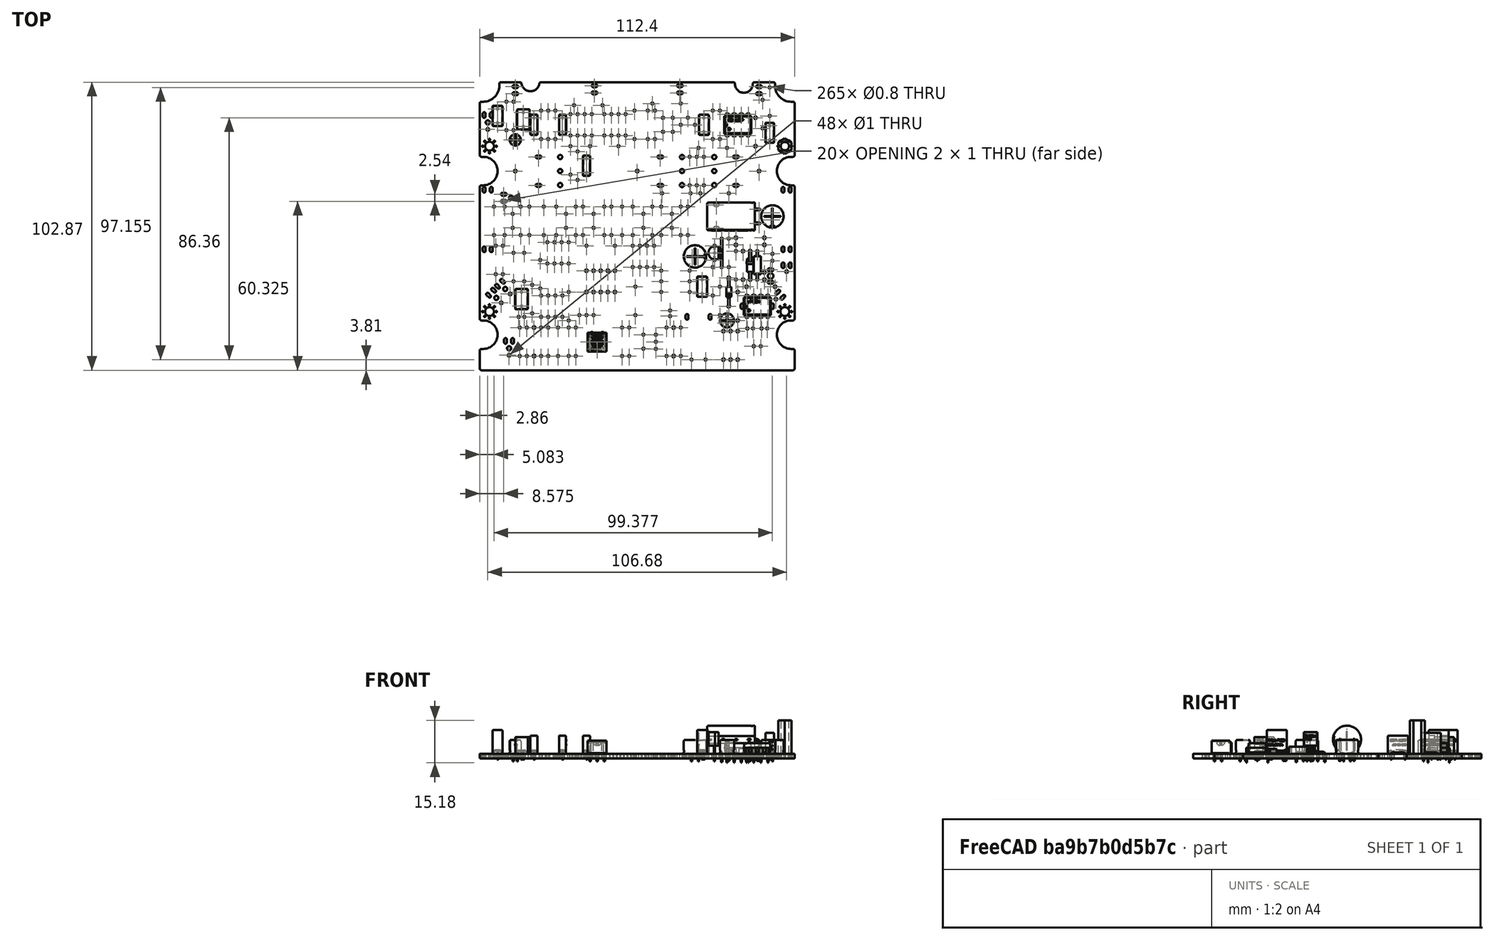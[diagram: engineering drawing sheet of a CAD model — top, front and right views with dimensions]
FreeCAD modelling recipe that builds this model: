
FCSTD DOCUMENT  (FreeCAD 0.19R17089 +1543 (Git))
Label: #100-000 - Phasor PCB Assembly
License: All rights reserved
LicenseURL: http://en.wikipedia.org/wiki/All_rights_reserved
objects: App::Link×103, Part::Feature×25, App::Part×7, PartDesign::CoordinateSystem×1, Sketcher::SketchObject×1
note: 27 computed .brp shape members not serialized (recipe doc carries the construction recipe); baked Part::Feature solids carry a one-line shape summary decoded from their .brp

FEATURE [PartDesign::CoordinateSystem] Local_CS_3323
  AttacherType = Attacher::AttachEngine3D
FEATURE [Part::Feature] Pcb_3323
  Placement = pos=(-147.637,134.62,0) rot=(0,0,1;0rad)
  shape: bbox 112.4 x 102.9 x 1.6 mm, 679 faces (baked)
FEATURE [Sketcher::SketchObject] PCB_Sketch_3323
  sketch-geometry (49):
    g0: LineSegment StartX=48.5775 StartY=90.17 StartZ=0 EndX=41.91 EndY=90.17 EndZ=0
    g1: LineSegment StartX=-41.91 StartY=90.17 StartZ=0 EndX=-48.5775 EndY=90.17 EndZ=0
    g2: LineSegment StartX=-56.1975 StartY=64.135 StartZ=0 EndX=-56.1975 EndY=82.55 EndZ=0
    g3: LineSegment StartX=56.1975 StartY=5.715 StartZ=0 EndX=56.1975 EndY=52.705 EndZ=0
    g4: LineSegment StartX=54.9275 StartY=53.34 StartZ=0 EndX=55.5625 EndY=53.34 EndZ=0
    g5: LineSegment StartX=54.9275 StartY=63.5 StartZ=0 EndX=55.5625 EndY=63.5 EndZ=0
    g6: LineSegment StartX=-54.9275 StartY=63.5 StartZ=0 EndX=-55.5625 EndY=63.5 EndZ=0
    g7: LineSegment StartX=-54.9275 StartY=53.34 StartZ=0 EndX=-55.5625 EndY=53.34 EndZ=0
    g8: LineSegment StartX=-54.9275 StartY=5.08 StartZ=0 EndX=-55.5625 EndY=5.08 EndZ=0
    g9: LineSegment StartX=49.2125 StartY=89.535 StartZ=0 EndX=49.2125 EndY=88.9 EndZ=0
    g10: LineSegment StartX=55.5625 StartY=83.185 StartZ=0 EndX=54.9275 EndY=83.185 EndZ=0
    g11: LineSegment StartX=55.5625 StartY=5.08 StartZ=0 EndX=54.9275 EndY=5.08 EndZ=0
    g12: LineSegment StartX=55.5625 StartY=-5.08 StartZ=0 EndX=54.9275 EndY=-5.08 EndZ=0
    g13: LineSegment StartX=-54.9275 StartY=-12.7 StartZ=0 EndX=-55.5625 EndY=-12.7 EndZ=0
    g14: LineSegment StartX=-54.9275 StartY=-5.08 StartZ=0 EndX=-55.5625 EndY=-5.08 EndZ=0
    g15: LineSegment StartX=-54.9275 StartY=83.185 StartZ=0 EndX=-55.5625 EndY=83.185 EndZ=0
    g16: LineSegment StartX=-49.2125 StartY=88.9 StartZ=0 EndX=-49.2125 EndY=89.535 EndZ=0
    g17: LineSegment StartX=-56.1975 StartY=-5.715 StartZ=0 EndX=-56.1975 EndY=-12.065 EndZ=0
    g18: LineSegment StartX=56.1975 StartY=-5.715 StartZ=0 EndX=56.1975 EndY=-12.065 EndZ=0
    g19: LineSegment StartX=34.29 StartY=90.17 StartZ=0 EndX=-34.29 EndY=90.17 EndZ=0
    g20: LineSegment StartX=56.1975 StartY=64.135 StartZ=0 EndX=56.1975 EndY=82.55 EndZ=0
    g21: LineSegment StartX=-54.9275 StartY=-12.7 StartZ=0 EndX=55.5625 EndY=-12.7 EndZ=0
    g22: LineSegment StartX=-56.1975 StartY=5.715 StartZ=0 EndX=-56.1975 EndY=52.705 EndZ=0
    g23: ArcOfCircle CenterX=-55.5625 CenterY=82.55 CenterZ=0 NormalX=0 NormalY=0 NormalZ=1 AngleXU=0 Radius=0.635 StartAngle=1.5708 EndAngle=3.14159
    g24: ArcOfCircle CenterX=-55.5625 CenterY=64.135 CenterZ=0 NormalX=0 NormalY=0 NormalZ=1 AngleXU=0 Radius=0.635 StartAngle=3.14159 EndAngle=4.71239
    g25: ArcOfCircle CenterX=-55.5625 CenterY=52.705 CenterZ=0 NormalX=0 NormalY=0 NormalZ=1 AngleXU=0 Radius=0.635 StartAngle=1.5708 EndAngle=3.14159
    g26: ArcOfCircle CenterX=-55.5625 CenterY=5.715 CenterZ=0 NormalX=0 NormalY=0 NormalZ=1 AngleXU=0 Radius=0.635 StartAngle=3.14159 EndAngle=4.71239
    g27: ArcOfCircle CenterX=-55.5625 CenterY=-5.715 CenterZ=0 NormalX=0 NormalY=0 NormalZ=1 AngleXU=0 Radius=0.635 StartAngle=1.5708 EndAngle=3.14159
    g28: ArcOfCircle CenterX=-55.5625 CenterY=-12.065 CenterZ=0 NormalX=0 NormalY=0 NormalZ=1 AngleXU=0 Radius=0.635 StartAngle=3.14159 EndAngle=4.71239
    g29: ArcOfCircle CenterX=55.5625 CenterY=-12.065 CenterZ=0 NormalX=0 NormalY=0 NormalZ=1 AngleXU=0 Radius=0.635 StartAngle=4.71239 EndAngle=6.28319
    g30: ArcOfCircle CenterX=55.5625 CenterY=-5.715 CenterZ=0 NormalX=0 NormalY=0 NormalZ=1 AngleXU=0 Radius=0.635 StartAngle=0 EndAngle=1.5708
    g31: ArcOfCircle CenterX=55.5625 CenterY=5.715 CenterZ=0 NormalX=0 NormalY=0 NormalZ=1 AngleXU=0 Radius=0.635 StartAngle=4.71239 EndAngle=6.28319
    g32: ArcOfCircle CenterX=55.5625 CenterY=52.705 CenterZ=0 NormalX=0 NormalY=0 NormalZ=1 AngleXU=0 Radius=0.635 StartAngle=0 EndAngle=1.5708
    g33: ArcOfCircle CenterX=55.5625 CenterY=64.135 CenterZ=0 NormalX=0 NormalY=0 NormalZ=1 AngleXU=0 Radius=0.635 StartAngle=4.71239 EndAngle=6.28319
    g34: ArcOfCircle CenterX=55.5625 CenterY=82.55 CenterZ=0 NormalX=0 NormalY=0 NormalZ=1 AngleXU=0 Radius=0.635 StartAngle=0 EndAngle=1.5708
    g35: ArcOfCircle CenterX=48.5775 CenterY=89.535 CenterZ=0 NormalX=0 NormalY=0 NormalZ=1 AngleXU=0 Radius=0.635 StartAngle=0 EndAngle=1.5708
    g36: ArcOfCircle CenterX=41.91 CenterY=89.535 CenterZ=0 NormalX=0 NormalY=0 NormalZ=1 AngleXU=0 Radius=0.635 StartAngle=1.5708 EndAngle=3.14159
    g37: ArcOfCircle CenterX=34.29 CenterY=89.535 CenterZ=0 NormalX=0 NormalY=0 NormalZ=1 AngleXU=0 Radius=0.635 StartAngle=0 EndAngle=1.5708
    g38: ArcOfCircle CenterX=-34.29 CenterY=89.535 CenterZ=0 NormalX=0 NormalY=0 NormalZ=1 AngleXU=0 Radius=0.635 StartAngle=1.5708 EndAngle=3.14159
    g39: ArcOfCircle CenterX=-41.91 CenterY=89.535 CenterZ=0 NormalX=0 NormalY=0 NormalZ=1 AngleXU=0 Radius=0.635 StartAngle=0 EndAngle=1.5708
    g40: ArcOfCircle CenterX=-48.5775 CenterY=89.535 CenterZ=0 NormalX=0 NormalY=0 NormalZ=1 AngleXU=0 Radius=0.635 StartAngle=1.5708 EndAngle=3.14159
    g41: ArcOfCircle CenterX=38.1 CenterY=89.535 CenterZ=0 NormalX=0 NormalY=0 NormalZ=1 AngleXU=0 Radius=3.175 StartAngle=3.14159 EndAngle=6.28319
    g42: ArcOfCircle CenterX=-38.1 CenterY=90.17 CenterZ=0 NormalX=0 NormalY=0 NormalZ=1 AngleXU=0 Radius=3.23788 StartAngle=3.33899 EndAngle=6.08579
    g43: ArcOfCircle CenterX=54.9275 CenterY=58.42 CenterZ=0 NormalX=0 NormalY=0 NormalZ=1 AngleXU=0 Radius=5.08 StartAngle=1.5708 EndAngle=4.71239
    g44: ArcOfCircle CenterX=-54.9275 CenterY=58.42 CenterZ=0 NormalX=0 NormalY=0 NormalZ=1 AngleXU=0 Radius=5.08 StartAngle=4.71239 EndAngle=7.85398
    g45: ArcOfCircle CenterX=54.9275 CenterY=0 CenterZ=0 NormalX=0 NormalY=0 NormalZ=1 AngleXU=0 Radius=5.08 StartAngle=1.5708 EndAngle=4.71239
    g46: ArcOfCircle CenterX=54.9275 CenterY=88.9 CenterZ=0 NormalX=0 NormalY=0 NormalZ=1 AngleXU=0 Radius=5.715 StartAngle=3.14159 EndAngle=4.71239
    g47: ArcOfCircle CenterX=-54.9275 CenterY=0 CenterZ=0 NormalX=0 NormalY=0 NormalZ=1 AngleXU=0 Radius=5.08 StartAngle=4.71239 EndAngle=7.85398
    g48: ArcOfCircle CenterX=-54.9275 CenterY=88.9 CenterZ=0 NormalX=0 NormalY=0 NormalZ=1 AngleXU=0 Radius=5.715 StartAngle=4.71239 EndAngle=6.28319
  constraints (49):
    c: Coincident(g17,g28)
    c: Coincident(g17,g27)
    c: Coincident(g22,g26)
    c: Coincident(g22,g25)
    c: Coincident(g24,g2)
    c: Coincident(g23,g2)
    c: Coincident(g28,g13)
    c: Coincident(g14,g27)
    c: Coincident(g8,g26)
    c: Coincident(g25,g7)
    c: Coincident(g6,g24)
    c: Coincident(g23,g15)
    c: Coincident(g21,g13)
    c: Coincident(g14,g47)
    c: Coincident(g8,g47)
    c: Coincident(g7,g44)
    c: Coincident(g6,g44)
    c: Coincident(g15,g48)
    c: Coincident(g48,g16)
    c: Coincident(g40,g16)
    c: Coincident(g40,g1)
    c: Coincident(g39,g1)
    c: Coincident(g39,g42)
    c: Coincident(g42,g38)
    c: Coincident(g19,g38)
    c: Coincident(g37,g19)
    c: Coincident(g37,g41)
    c: Coincident(g41,g36)
    c: Coincident(g0,g36)
    c: Coincident(g35,g0)
    c: Coincident(g9,g46)
    c: Coincident(g35,g9)
    c: Coincident(g12,g45)
    c: Coincident(g45,g11)
    c: Coincident(g4,g43)
    c: Coincident(g43,g5)
    c: Coincident(g10,g46)
    c: Coincident(g21,g29)
    c: Coincident(g30,g12)
    c: Coincident(g31,g11)
    c: Coincident(g4,g32)
    c: Coincident(g33,g5)
    c: Coincident(g34,g10)
    c: Coincident(g18,g29)
    c: Coincident(g18,g30)
    c: Coincident(g31,g3)
    c: Coincident(g3,g32)
    c: Coincident(g20,g33)
    c: Coincident(g20,g34)
FEATURE [App::Part] Board_Geoms_3323
  Group = -> [Local_CS_3323,Pcb_3323,PCB_Sketch_3323]
  Origin = -> Origin
FEATURE [Part::Feature] Shape  label=""Z6"_RC4558P_5E32D110"
  Placement = pos=(35.8775,74.93,0) rot=(0,0,1;1.5708rad)
  shape: bbox 9.59 x 7.87 x 7.1 mm, 280 faces (baked)
FEATURE [App::Link] _Z6__RC4558P_5E32D110_ln_  label=""Z2"_RC4558P_5E32CA1D"
  LinkPlacement = pos=(-28.2575,29.21,0) rot=(0,0,1;1.5708rad)
  LinkedObject = -> Shape
  Placement = pos=(-28.2575,29.21,0) rot=(0,0,1;1.5708rad)
FEATURE [App::Link] _Z6__RC4558P_5E32D110_ln_001  label=""Z1"_RC4558P_5E32C91E"
  LinkPlacement = pos=(-20.0025,74.93,0) rot=(0,0,1;1.5708rad)
  LinkedObject = -> Shape
  Placement = pos=(-20.0025,74.93,0) rot=(0,0,1;1.5708rad)
FEATURE [Part::Feature] Shape003  label=""XR5"_R_CC25_P10.16_H_5E176B90"
  Placement = pos=(42.8625,24.765,0) rot=(0,0,-1;1.5708rad)
  shape: bbox 2.5 x 10.96 x 5.1 mm, 11 faces (baked)
FEATURE [App::Link] _Z6__RC4558P_5E32D110_ln_002  label=""Z4"_RC4558P_5E30B0B1"
  LinkPlacement = pos=(-7.9375,74.93,0) rot=(0,0,1;1.5708rad)
  LinkedObject = -> Shape
  Placement = pos=(-7.9375,74.93,0) rot=(0,0,1;1.5708rad)
FEATURE [App::Link] _Z6__RC4558P_5E32D110_ln_003  label=""Z3"_RC4558P_5E27DE26"
  LinkPlacement = pos=(2.2225,27.94,0) rot=(0,0,1;1.5708rad)
  LinkedObject = -> Shape
  Placement = pos=(2.2225,27.94,0) rot=(0,0,1;1.5708rad)
FEATURE [Part::Feature] Shape004  label=""JP16"_R_0R_Wire_Jumper_P10.16_5D8DF354"
  Placement = pos=(30.1625,29.21,0) rot=(0,0,1;1.5708rad)
  shape: bbox 0.55 x 10.88 x 3.709 mm, 7 faces (baked)
FEATURE [App::Link] _JP16__R_0R_Wire_Jumper_P10_16_5D8DF354_ln_  label=""JP15"_R_0R_Wire_Jumper_P10.16_5DC241EA"
  LinkPlacement = pos=(13.6525,15.24,0) rot=(0,0,1;3.14159rad)
  LinkedObject = -> Shape004
  Placement = pos=(13.6525,15.24,0) rot=(0,0,1;3.14159rad)
FEATURE [App::Link] _JP16__R_0R_Wire_Jumper_P10_16_5D8DF354_ln_001  label=""JP14"_R_0R_Wire_Jumper_P10.16_5DC2C7B0"
  LinkPlacement = pos=(26.9875,19.05,0) rot=(0,0,1;1.5708rad)
  LinkedObject = -> Shape004
  Placement = pos=(26.9875,19.05,0) rot=(0,0,1;1.5708rad)
FEATURE [App::Link] _JP16__R_0R_Wire_Jumper_P10_16_5D8DF354_ln_002  label=""JP13"_R_0R_Wire_Jumper_P10.16_5DC188E7"
  LinkPlacement = pos=(13.6525,19.05,0) rot=(0,0,1;3.14159rad)
  LinkedObject = -> Shape004
  Placement = pos=(13.6525,19.05,0) rot=(0,0,1;3.14159rad)
FEATURE [App::Link] _JP16__R_0R_Wire_Jumper_P10_16_5D8DF354_ln_003  label=""JP12"_R_0R_Wire_Jumper_P10.16_5D8C3305"
  LinkPlacement = pos=(-0.635,12.065,0) rot=(0,0,-1;1.5708rad)
  LinkedObject = -> Shape004
  Placement = pos=(-0.635,12.065,0) rot=(0,0,-1;1.5708rad)
FEATURE [App::Link] _JP16__R_0R_Wire_Jumper_P10_16_5D8DF354_ln_004  label=""JP11"_R_0R_Wire_Jumper_P10.16_5D8B2677"
  LinkPlacement = pos=(-24.4475,10.16,0) rot=(0,0,1;1.5708rad)
  LinkedObject = -> Shape004
  Placement = pos=(-24.4475,10.16,0) rot=(0,0,1;1.5708rad)
FEATURE [App::Link] _JP16__R_0R_Wire_Jumper_P10_16_5D8DF354_ln_005  label=""JP10"_R_0R_Wire_Jumper_P10.16_5D8B2701"
  LinkPlacement = pos=(27.6225,50.4825,0) rot=(0,0,1;3.14159rad)
  LinkedObject = -> Shape004
  Placement = pos=(27.6225,50.4825,0) rot=(0,0,1;3.14159rad)
FEATURE [App::Link] _JP16__R_0R_Wire_Jumper_P10_16_5D8DF354_ln_006  label=""JP9"_R_0R_Wire_Jumper_P10.16_5DD3D00C"
  LinkPlacement = pos=(13.97,50.4825,0) rot=(0,0,1;3.14159rad)
  LinkedObject = -> Shape004
  Placement = pos=(13.97,50.4825,0) rot=(0,0,1;3.14159rad)
FEATURE [App::Link] _JP16__R_0R_Wire_Jumper_P10_16_5D8DF354_ln_007  label=""JP8"_R_0R_Wire_Jumper_P10.16_5DC072A0"
  LinkPlacement = pos=(-11.7475,67.31,0) rot=(0,0,1;0rad)
  LinkedObject = -> Shape004
  Placement = pos=(-11.7475,67.31,0) rot=(0,0,1;0rad)
FEATURE [App::Link] _JP16__R_0R_Wire_Jumper_P10_16_5D8DF354_ln_008  label=""JP7"_R_0R_Wire_Jumper_P10.16_5DC277DA"
  LinkPlacement = pos=(29.5275,12.065,0) rot=(0,0,1;1.5708rad)
  LinkedObject = -> Shape004
  Placement = pos=(29.5275,12.065,0) rot=(0,0,1;1.5708rad)
FEATURE [App::Link] _JP16__R_0R_Wire_Jumper_P10_16_5D8DF354_ln_009  label=""JP6"_R_0R_Wire_Jumper_P10.16_5DC20B18"
  LinkPlacement = pos=(13.6525,22.86,0) rot=(0,0,1;0rad)
  LinkedObject = -> Shape004
  Placement = pos=(13.6525,22.86,0) rot=(0,0,1;0rad)
FEATURE [App::Link] _JP16__R_0R_Wire_Jumper_P10_16_5D8DF354_ln_010  label=""JP5"_R_0R_Wire_Jumper_P10.16_5D8B268E"
  LinkPlacement = pos=(-13.0175,31.75,0) rot=(0,0,1;3.14159rad)
  LinkedObject = -> Shape004
  Placement = pos=(-13.0175,31.75,0) rot=(0,0,1;3.14159rad)
FEATURE [App::Link] _JP16__R_0R_Wire_Jumper_P10_16_5D8DF354_ln_011  label=""JP4"_R_0R_Wire_Jumper_P10.16_5D8B2660"
  LinkPlacement = pos=(-34.6075,21.59,0) rot=(0,0,1;1.5708rad)
  LinkedObject = -> Shape004
  Placement = pos=(-34.6075,21.59,0) rot=(0,0,1;1.5708rad)
FEATURE [App::Link] _JP16__R_0R_Wire_Jumper_P10_16_5D8DF354_ln_012  label=""JP3"_R_0R_Wire_Jumper_P10.16_5DD3B88C"
  LinkPlacement = pos=(26.9875,66.675,0) rot=(0,0,1;0rad)
  LinkedObject = -> Shape004
  Placement = pos=(26.9875,66.675,0) rot=(0,0,1;0rad)
FEATURE [App::Link] _JP16__R_0R_Wire_Jumper_P10_16_5D8DF354_ln_013  label=""JP2"_R_0R_Wire_Jumper_P10.16_5DC16F9F"
  LinkPlacement = pos=(10.4775,82.55,0) rot=(0,0,1;0rad)
  LinkedObject = -> Shape004
  Placement = pos=(10.4775,82.55,0) rot=(0,0,1;0rad)
FEATURE [App::Link] _JP16__R_0R_Wire_Jumper_P10_16_5D8DF354_ln_014  label=""JP1"_R_0R_Wire_Jumper_P10.16_5DC0E925"
  LinkPlacement = pos=(-17.4625,81.915,0) rot=(0,0,1;0rad)
  LinkedObject = -> Shape004
  Placement = pos=(-17.4625,81.915,0) rot=(0,0,1;0rad)
FEATURE [App::Link] _Z6__RC4558P_5E32D110_ln_004  label=""Z5"_RC4558P_5E251C84"
  LinkPlacement = pos=(-30.48,10.16,0) rot=(0,0,1;1.5708rad)
  LinkedObject = -> Shape
  Placement = pos=(-30.48,10.16,0) rot=(0,0,1;1.5708rad)
FEATURE [Part::Feature] Shape005  label=""XU1"_LT1054_5DC00D2F"
  Placement = pos=(42.8625,10.16,0) rot=(0,0,1;1.5708rad)
  shape: bbox 9.59 x 7.87 x 7.1 mm, 205 faces (baked)
FEATURE [Part::Feature] Shape007  label=""RV52"_Bourns_3362P_5D8A0BC8"
  Placement = pos=(-14.2875,-2.54,0) rot=(0,0,1;3.14159rad)
  shape: bbox 6.706 x 7.036 x 7.295 mm, 550 faces (baked)
FEATURE [App::Link] _RV52__Bourns_3362P_5D8A0BC8_ln_  label=""RV51"_Bourns_3362P_5DCDF837"
  LinkPlacement = pos=(18.0975,74.93,0) rot=(0,0,1;0rad)
  LinkedObject = -> Shape007
  Placement = pos=(18.0975,74.93,0) rot=(0,0,1;0rad)
FEATURE [Part::Feature] Shape008  label=""XD11"_DO-35_P10.16_5DC00C72"
  Placement = pos=(32.7025,15.24,0) rot=(0,0,-1;1.5708rad)
  shape: bbox 1.862 x 10.84 x 4.391 mm, 17 faces (baked)
FEATURE [App::Link] _XD11__DO_35_P10_16_5DC00C72_ln_  label=""XD10"_DO-35_P10.16_5DC00C63"
  LinkPlacement = pos=(13.0175,-2.54,0) rot=(0,0,1;1.5708rad)
  LinkedObject = -> Shape008
  Placement = pos=(13.0175,-2.54,0) rot=(0,0,1;1.5708rad)
FEATURE [App::Link] _XD11__DO_35_P10_16_5DC00C72_ln_001  label=""D9"_DO-35_P10.16_5E2AA1CA"
  LinkPlacement = pos=(-36.83,-2.54,0) rot=(0,0,1;1.5708rad)
  LinkedObject = -> Shape008
  Placement = pos=(-36.83,-2.54,0) rot=(0,0,1;1.5708rad)
FEATURE [App::Link] _XD11__DO_35_P10_16_5DC00C72_ln_002  label=""D8"_DO-35_P10.16_5DD3B6E0"
  LinkPlacement = pos=(42.2275,72.39,0) rot=(0,0,1;1.5708rad)
  LinkedObject = -> Shape008
  Placement = pos=(42.2275,72.39,0) rot=(0,0,1;1.5708rad)
FEATURE [App::Link] _XR5__R_CC25_P10_16_H_5E176B90_ln_  label=""XR4"_R_CC25_P10.16_H_5DCF4C98"
  LinkPlacement = pos=(35.2425,24.765,0) rot=(0,0,1;1.5708rad)
  LinkedObject = -> Shape003
  Placement = pos=(35.2425,24.765,0) rot=(0,0,1;1.5708rad)
FEATURE [App::Link] _XR5__R_CC25_P10_16_H_5E176B90_ln_001  label=""XR3"_R_CC25_P10.16_H_5DD0A4F3"
  LinkPlacement = pos=(10.4775,-2.54,0) rot=(0,0,1;1.5708rad)
  LinkedObject = -> Shape003
  Placement = pos=(10.4775,-2.54,0) rot=(0,0,1;1.5708rad)
FEATURE [Part::Feature] Shape010  label=""XC10"_Nichicon_UMA_Straight_D8_H5_P2.5_d0.45_LL2.6_5DC00BE9"
  Placement = pos=(20.6375,27.94,0) rot=(0,0,1;0rad)
  shape: bbox 8.659 x 8.659 x 7.61 mm, 57 faces (baked)
FEATURE [App::Link] _XC10__Nichicon_UMA_Straight_D8_H5_P2_5_d0_45_LL2_6_5DC00BE9_ln_  label=""XC9"_Nichicon_UMA_Straight_D8_H5_P2.5_d0.45_LL2.6_5DC00BB3"
  LinkPlacement = pos=(11.7475,7.62,0) rot=(0,0,1;1.5708rad)
  LinkedObject = -> Shape010
  Placement = pos=(11.7475,7.62,0) rot=(0,0,1;1.5708rad)
FEATURE [Part::Feature] Shape011  label=""XC12"_FKS2G021001C00KSSD_5DC00BFC"
  Placement = pos=(23.1775,17.145,0) rot=(0,0,1;1.5708rad)
  shape: bbox 4.65 x 15.3 x 10.5 mm, 403 faces (baked)
FEATURE [App::Link] _XC12__FKS2G021001C00KSSD_5DC00BFC_ln_  label=""XC11"_FKS2G021001C00KSSD_5DC00BC6"
  LinkPlacement = pos=(2.2225,-2.5,0) rot=(0,0,-1;1.5708rad)
  LinkedObject = -> Shape011
  Placement = pos=(2.2225,-2.5,0) rot=(0,0,-1;1.5708rad)
FEATURE [Part::Feature] Shape012  label=""XC8"_Capacitor_Electrolytic_THT_Radial_Angled_D10_H17_P5_d0.6_h1.5_LL2.6_5E35ED22"
  Placement = pos=(43.4975,42.2275,0) rot=(0,0,1;1.5708rad)
  shape: bbox 18.92 x 10.82 x 13.01 mm, 66 faces (baked)
FEATURE [App::Link] _XC8__Capacitor_Electrolytic_THT_Radial_Angled_D10_H17_P5_d0_6_h1_5_LL2_6_5E35ED22_ln_  label=""XC7"_Capacitor_Electrolytic_THT_Radial_Angled_D10_H17_P5_d0.6_h1.5_LL2.6_5DC00BAC"
  LinkPlacement = pos=(21.9075,-8.89,0) rot=(0,0,1;0rad)
  LinkedObject = -> Shape012
  Placement = pos=(21.9075,-8.89,0) rot=(0,0,1;0rad)
FEATURE [Part::Feature] Shape013  label=""C14"_FKP2J008201D00HSSD_5D8C32AA"
  Placement = pos=(-41.275,12.7,0) rot=(0,0,-1;1.5708rad)
  shape: bbox 6.15 x 15.3 x 8 mm, 422 faces (baked)
FEATURE [Part::Feature] Shape014  label=""C2"_FKP2O100331D00JSSD_5DED6ED0"
  Placement = pos=(-40.64,76.835,0) rot=(0,0,-1;1.5708rad)
  shape: bbox 6.15 x 15.3 x 8 mm, 367 faces (baked)
FEATURE [Part::Feature] Shape015  label=""XC6"_Nichicon_UMA_Straight_D8_H5_P2.5_d0.45_LL2.6_5DCF4B87"
  Placement = pos=(48.26,42.2275,0) rot=(0,0,-1;1.5708rad)
  shape: bbox 8.659 x 8.659 x 7.61 mm, 57 faces (baked)
FEATURE [App::Link] _XC6__Nichicon_UMA_Straight_D8_H5_P2_5_d0_45_LL2_6_5DCF4B87_ln_  label=""XC5"_Nichicon_UMA_Straight_D8_H5_P2.5_d0.45_LL2.6_5E298AA2"
  LinkPlacement = pos=(48.26,27.6225,0) rot=(0,0,-1;1.5708rad)
  LinkedObject = -> Shape015
  Placement = pos=(48.26,27.6225,0) rot=(0,0,-1;1.5708rad)
FEATURE [Part::Feature] Shape016  label=""XC3"_Nichicon_UMA_Straight_D5_H5_P2_d0.45_LL2.6_5DC00C0A"
  Placement = pos=(32.0675,5.08,0) rot=(0,0,1;1.5708rad)
  shape: bbox 5.412 x 5.412 x 7.61 mm, 57 faces (baked)
FEATURE [App::Link] _XC3__Nichicon_UMA_Straight_D5_H5_P2_d0_45_LL2_6_5DC00C0A_ln_  label=""XC2"_Nichicon_UMA_Straight_D5_H5_P2_d0.45_LL2.6_5DC00C03"
  LinkPlacement = pos=(45.4025,2.2225,0) rot=(0,0,1;0rad)
  LinkedObject = -> Shape016
  Placement = pos=(45.4025,2.2225,0) rot=(0,0,1;0rad)
FEATURE [App::Link] _XC3__Nichicon_UMA_Straight_D5_H5_P2_d0_45_LL2_6_5DC00C0A_ln_001  label=""XC1"_Nichicon_UMA_Straight_D5_H5_P2_d0.45_LL2.6_5DC00BCD"
  LinkPlacement = pos=(40.3225,2.2225,0) rot=(0,0,1;0rad)
  LinkedObject = -> Shape016
  Placement = pos=(40.3225,2.2225,0) rot=(0,0,1;0rad)
FEATURE [App::Link] _XC6__Nichicon_UMA_Straight_D8_H5_P2_5_d0_45_LL2_6_5DCF4B87_ln_001  label=""XC4"_Nichicon_UMA_Straight_D8_H5_P2.5_d0.45_LL2.6_5DC00B97"
  LinkPlacement = pos=(42.8625,-4.1275,0) rot=(0,0,1;0rad)
  LinkedObject = -> Shape015
  Placement = pos=(42.8625,-4.1275,0) rot=(0,0,1;0rad)
FEATURE [App::Link] _XC3__Nichicon_UMA_Straight_D5_H5_P2_d0_45_LL2_6_5DC00C0A_ln_002  label=""C15"_Nichicon_UMA_Straight_D5_H5_P2_d0.45_LL2.6_5E2AA272"
  LinkPlacement = pos=(-41.275,6.35,0) rot=(0,0,1;0rad)
  LinkedObject = -> Shape016
  Placement = pos=(-41.275,6.35,0) rot=(0,0,1;0rad)
FEATURE [Part::Feature] Shape017  label=""C13"_Nichicon_UMA_Straight_D4_H5_P1.5_d0.45_LL2.6_5D8A0658"
  Placement = pos=(-43.4975,69.5325,0) rot=(0,0,1;3.14159rad)
  shape: bbox 4.33 x 4.33 x 7.61 mm, 61 faces (baked)
FEATURE [App::Link] _XR5__R_CC25_P10_16_H_5E176B90_ln_002  label=""XR2"_R_CC25_P10.16_H_5DCFCEA2"
  LinkPlacement = pos=(32.7025,29.21,0) rot=(0,0,1;1.5708rad)
  LinkedObject = -> Shape003
  Placement = pos=(32.7025,29.21,0) rot=(0,0,1;1.5708rad)
FEATURE [App::Link] _XR5__R_CC25_P10_16_H_5E176B90_ln_003  label=""XR1"_R_CC25_P10.16_H_5DC00CFC"
  LinkPlacement = pos=(15.5575,-2.54,0) rot=(0,0,-1;1.5708rad)
  LinkedObject = -> Shape003
  Placement = pos=(15.5575,-2.54,0) rot=(0,0,-1;1.5708rad)
FEATURE [App::Link] _XR5__R_CC25_P10_16_H_5E176B90_ln_004  label=""YR2"_R_CC25_P10.16_H_5E2AA297"
  LinkPlacement = pos=(-39.37,-2.54,0) rot=(0,0,-1;1.5708rad)
  LinkedObject = -> Shape003
  Placement = pos=(-39.37,-2.54,0) rot=(0,0,-1;1.5708rad)
FEATURE [App::Link] _XR5__R_CC25_P10_16_H_5E176B90_ln_005  label=""YR1"_R_CC25_P10.16_H_5DD10E25"
  LinkPlacement = pos=(-51.1175,40.64,0) rot=(0,0,1;1.5708rad)
  LinkedObject = -> Shape003
  Placement = pos=(-51.1175,40.64,0) rot=(0,0,1;1.5708rad)
FEATURE [App::Link] _XR5__R_CC25_P10_16_H_5E176B90_ln_006  label=""R57"_R_CC25_P10.16_H_5E2EAABC"
  LinkPlacement = pos=(47.3075,83.185,0) rot=(0,0,-1;1.5708rad)
  LinkedObject = -> Shape003
  Placement = pos=(47.3075,83.185,0) rot=(0,0,-1;1.5708rad)
FEATURE [App::Link] _XR5__R_CC25_P10_16_H_5E176B90_ln_007  label=""R56"_R_CC25_P10.16_H_5E2EB080"
  LinkPlacement = pos=(44.7675,78.74,0) rot=(0,0,-1;1.5708rad)
  LinkedObject = -> Shape003
  Placement = pos=(44.7675,78.74,0) rot=(0,0,-1;1.5708rad)
FEATURE [App::Link] _XR5__R_CC25_P10_16_H_5E176B90_ln_008  label=""R45"_R_CC25_P10.16_H_5D8A0B22"
  LinkPlacement = pos=(-21.9075,-2.54,0) rot=(0,0,-1;1.5708rad)
  LinkedObject = -> Shape003
  Placement = pos=(-21.9075,-2.54,0) rot=(0,0,-1;1.5708rad)
FEATURE [App::Link] _XR5__R_CC25_P10_16_H_5E176B90_ln_009  label=""R44"_R_CC25_P10.16_H_5E2AA249"
  LinkPlacement = pos=(-34.29,-2.54,0) rot=(0,0,-1;1.5708rad)
  LinkedObject = -> Shape003
  Placement = pos=(-34.29,-2.54,0) rot=(0,0,-1;1.5708rad)
FEATURE [App::Link] _XR5__R_CC25_P10_16_H_5E176B90_ln_010  label=""R43"_R_CC25_P10.16_H_5D8A0AF4"
  LinkPlacement = pos=(-24.4475,-2.54,0) rot=(0,0,-1;1.5708rad)
  LinkedObject = -> Shape003
  Placement = pos=(-24.4475,-2.54,0) rot=(0,0,-1;1.5708rad)
FEATURE [App::Link] _XR5__R_CC25_P10_16_H_5E176B90_ln_011  label=""R42"_R_CC25_P10.16_H_5E2AA2C4"
  LinkPlacement = pos=(-31.75,-2.54,0) rot=(0,0,-1;1.5708rad)
  LinkedObject = -> Shape003
  Placement = pos=(-31.75,-2.54,0) rot=(0,0,-1;1.5708rad)
FEATURE [App::Link] _XR5__R_CC25_P10_16_H_5E176B90_ln_012  label=""R41"_R_CC25_P10.16_H_5D8A0AC6"
  LinkPlacement = pos=(-28.2575,-2.54,0) rot=(0,0,-1;1.5708rad)
  LinkedObject = -> Shape003
  Placement = pos=(-28.2575,-2.54,0) rot=(0,0,-1;1.5708rad)
FEATURE [App::Link] _XR5__R_CC25_P10_16_H_5E176B90_ln_013  label=""R39"_R_CC25_P10.16_H_5D8A0AAF"
  LinkPlacement = pos=(-5.3975,-2.54,0) rot=(0,0,-1;1.5708rad)
  LinkedObject = -> Shape003
  Placement = pos=(-5.3975,-2.54,0) rot=(0,0,-1;1.5708rad)
FEATURE [App::Link] _XR5__R_CC25_P10_16_H_5E176B90_ln_014  label=""R37"_R_CC25_P10.16_H_5D8A0A98"
  LinkPlacement = pos=(-2.8575,-2.54,0) rot=(0,0,-1;1.5708rad)
  LinkedObject = -> Shape003
  Placement = pos=(-2.8575,-2.54,0) rot=(0,0,-1;1.5708rad)
FEATURE [App::Link] _XR5__R_CC25_P10_16_H_5E176B90_ln_015  label=""R36"_R_CC25_P10.16_H_5D8A0A81"
  LinkPlacement = pos=(18.7325,58.42,0) rot=(0,0,-1;1.5708rad)
  LinkedObject = -> Shape003
  Placement = pos=(18.7325,58.42,0) rot=(0,0,-1;1.5708rad)
FEATURE [App::Link] _XR5__R_CC25_P10_16_H_5E176B90_ln_016  label=""R35"_R_CC25_P10.16_H_5D8A0A6A"
  LinkPlacement = pos=(23.8125,58.42,0) rot=(0,0,-1;1.5708rad)
  LinkedObject = -> Shape003
  Placement = pos=(23.8125,58.42,0) rot=(0,0,-1;1.5708rad)
FEATURE [App::Link] _XR5__R_CC25_P10_16_H_5E176B90_ln_017  label=""R34"_R_CC25_P10.16_H_5D8A0A53"
  LinkPlacement = pos=(21.2725,58.42,0) rot=(0,0,-1;1.5708rad)
  LinkedObject = -> Shape003
  Placement = pos=(21.2725,58.42,0) rot=(0,0,-1;1.5708rad)
FEATURE [App::Link] _XR5__R_CC25_P10_16_H_5E176B90_ln_018  label=""R33"_R_CC25_P10.16_H_5D8A0A3C"
  LinkPlacement = pos=(29.5275,74.93,0) rot=(0,0,1;1.5708rad)
  LinkedObject = -> Shape003
  Placement = pos=(29.5275,74.93,0) rot=(0,0,1;1.5708rad)
FEATURE [App::Link] _XR5__R_CC25_P10_16_H_5E176B90_ln_019  label=""R32"_R_CC25_P10.16_H_5D8A0A25"
  LinkPlacement = pos=(26.9875,74.93,0) rot=(0,0,-1;1.5708rad)
  LinkedObject = -> Shape003
  Placement = pos=(26.9875,74.93,0) rot=(0,0,-1;1.5708rad)
FEATURE [App::Link] _XR5__R_CC25_P10_16_H_5E176B90_ln_020  label=""R31"_R_CC25_P10.16_H_5E2AA1F5"
  LinkPlacement = pos=(-41.91,-2.54,0) rot=(0,0,-1;1.5708rad)
  LinkedObject = -> Shape003
  Placement = pos=(-41.91,-2.54,0) rot=(0,0,-1;1.5708rad)
FEATURE [App::Link] _XR5__R_CC25_P10_16_H_5E176B90_ln_021  label=""R30"_R_CC25_P10.16_H_5DF72136"
  LinkPlacement = pos=(-37.465,12.7,0) rot=(0,0,1;1.5708rad)
  LinkedObject = -> Shape003
  Placement = pos=(-37.465,12.7,0) rot=(0,0,1;1.5708rad)
FEATURE [App::Link] _XR5__R_CC25_P10_16_H_5E176B90_ln_022  label=""R29"_R_CC25_P10.16_H_5D8A09E0"
  LinkPlacement = pos=(-47.9425,26.67,0) rot=(0,0,-1;1.5708rad)
  LinkedObject = -> Shape003
  Placement = pos=(-47.9425,26.67,0) rot=(0,0,-1;1.5708rad)
FEATURE [App::Link] _XR5__R_CC25_P10_16_H_5E176B90_ln_023  label=""R28"_R_CC25_P10.16_H_5D8A09C9"
  LinkPlacement = pos=(-50.4825,26.67,0) rot=(0,0,1;1.5708rad)
  LinkedObject = -> Shape003
  Placement = pos=(-50.4825,26.67,0) rot=(0,0,1;1.5708rad)
FEATURE [App::Link] _XR5__R_CC25_P10_16_H_5E176B90_ln_024  label=""R27"_R_CC25_P10.16_H_5D8A09B2"
  LinkPlacement = pos=(-44.1325,24.13,0) rot=(0,0,1;1.5708rad)
  LinkedObject = -> Shape003
  Placement = pos=(-44.1325,24.13,0) rot=(0,0,1;1.5708rad)
FEATURE [App::Link] _XR5__R_CC25_P10_16_H_5E176B90_ln_025  label=""R26"_R_CC25_P10.16_H_5D8A099B"
  LinkPlacement = pos=(-40.3225,24.13,0) rot=(0,0,1;1.5708rad)
  LinkedObject = -> Shape003
  Placement = pos=(-40.3225,24.13,0) rot=(0,0,1;1.5708rad)
FEATURE [App::Link] _XR5__R_CC25_P10_16_H_5E176B90_ln_026  label=""R25"_R_CC25_P10.16_H_5D8B716B"
  LinkPlacement = pos=(18.0975,40.64,0) rot=(0,0,-1;1.5708rad)
  LinkedObject = -> Shape003
  Placement = pos=(18.0975,40.64,0) rot=(0,0,-1;1.5708rad)
FEATURE [App::Link] _XR5__R_CC25_P10_16_H_5E176B90_ln_027  label=""R24"_R_CC25_P10.16_H_5D8A096D"
  LinkPlacement = pos=(6.35,74.93,0) rot=(0,0,1;1.5708rad)
  LinkedObject = -> Shape003
  Placement = pos=(6.35,74.93,0) rot=(0,0,1;1.5708rad)
FEATURE [App::Link] _XR5__R_CC25_P10_16_H_5E176B90_ln_028  label=""R23"_R_CC25_P10.16_H_5D8A0956"
  LinkPlacement = pos=(3.81,74.93,0) rot=(0,0,-1;1.5708rad)
  LinkedObject = -> Shape003
  Placement = pos=(3.81,74.93,0) rot=(0,0,-1;1.5708rad)
FEATURE [App::Link] _XR5__R_CC25_P10_16_H_5E176B90_ln_029  label=""R22"_R_CC25_P10.16_H_5D8B6ED7"
  LinkPlacement = pos=(15.5575,40.64,0) rot=(0,0,-1;1.5708rad)
  LinkedObject = -> Shape003
  Placement = pos=(15.5575,40.64,0) rot=(0,0,-1;1.5708rad)
FEATURE [App::Link] _XR5__R_CC25_P10_16_H_5E176B90_ln_030  label=""R21"_R_CC25_P10.16_H_5D8A0928"
  LinkPlacement = pos=(-0.9525,74.93,0) rot=(0,0,-1;1.5708rad)
  LinkedObject = -> Shape003
  Placement = pos=(-0.9525,74.93,0) rot=(0,0,-1;1.5708rad)
FEATURE [App::Link] _XR5__R_CC25_P10_16_H_5E176B90_ln_031  label=""R20"_R_CC25_P10.16_H_5D8B7021"
  LinkPlacement = pos=(8.5725,40.64,0) rot=(0,0,-1;1.5708rad)
  LinkedObject = -> Shape003
  Placement = pos=(8.5725,40.64,0) rot=(0,0,-1;1.5708rad)
FEATURE [App::Link] _XR5__R_CC25_P10_16_H_5E176B90_ln_032  label=""R19"_R_CC25_P10.16_H_5D8C3024"
  LinkPlacement = pos=(5.3975,40.64,0) rot=(0,0,1;1.5708rad)
  LinkedObject = -> Shape003
  Placement = pos=(5.3975,40.64,0) rot=(0,0,1;1.5708rad)
FEATURE [App::Link] _XR5__R_CC25_P10_16_H_5E176B90_ln_033  label=""R18"_R_CC25_P10.16_H_5D8B70E7"
  LinkPlacement = pos=(-1.5875,40.64,0) rot=(0,0,-1;1.5708rad)
  LinkedObject = -> Shape003
  Placement = pos=(-1.5875,40.64,0) rot=(0,0,-1;1.5708rad)
FEATURE [App::Link] _XR5__R_CC25_P10_16_H_5E176B90_ln_034  label=""R17"_R_CC25_P10.16_H_5D8B6E95"
  LinkPlacement = pos=(-5.3975,40.64,0) rot=(0,0,-1;1.5708rad)
  LinkedObject = -> Shape003
  Placement = pos=(-5.3975,40.64,0) rot=(0,0,-1;1.5708rad)
FEATURE [App::Link] _XR5__R_CC25_P10_16_H_5E176B90_ln_035  label=""R16"_R_CC25_P10.16_H_5D8B6F9D"
  LinkPlacement = pos=(-11.7475,40.64,0) rot=(0,0,1;1.5708rad)
  LinkedObject = -> Shape003
  Placement = pos=(-11.7475,40.64,0) rot=(0,0,1;1.5708rad)
FEATURE [App::Link] _XR5__R_CC25_P10_16_H_5E176B90_ln_036  label=""R15"_R_CC25_P10.16_H_5D8B6FDF"
  LinkPlacement = pos=(-9.2075,40.64,0) rot=(0,0,-1;1.5708rad)
  LinkedObject = -> Shape003
  Placement = pos=(-9.2075,40.64,0) rot=(0,0,-1;1.5708rad)
FEATURE [App::Link] _XR5__R_CC25_P10_16_H_5E176B90_ln_037  label=""R14"_R_CC25_P10.16_H_5D8B7063"
  LinkPlacement = pos=(-19.3675,40.64,0) rot=(0,0,-1;1.5708rad)
  LinkedObject = -> Shape003
  Placement = pos=(-19.3675,40.64,0) rot=(0,0,-1;1.5708rad)
FEATURE [App::Link] _XR5__R_CC25_P10_16_H_5E176B90_ln_038  label=""R13"_R_CC25_P10.16_H_5D8B7129"
  LinkPlacement = pos=(-21.9075,40.64,0) rot=(0,0,1;1.5708rad)
  LinkedObject = -> Shape003
  Placement = pos=(-21.9075,40.64,0) rot=(0,0,1;1.5708rad)
FEATURE [App::Link] _XR5__R_CC25_P10_16_H_5E176B90_ln_039  label=""R12"_R_CC25_P10.16_H_5D8B70A5"
  LinkPlacement = pos=(-28.8925,40.64,0) rot=(0,0,-1;1.5708rad)
  LinkedObject = -> Shape003
  Placement = pos=(-28.8925,40.64,0) rot=(0,0,-1;1.5708rad)
FEATURE [App::Link] _XR5__R_CC25_P10_16_H_5E176B90_ln_040  label=""R11"_R_CC25_P10.16_H_5DD42A9D"
  LinkPlacement = pos=(-33.3375,40.64,0) rot=(0,0,-1;1.5708rad)
  LinkedObject = -> Shape003
  Placement = pos=(-33.3375,40.64,0) rot=(0,0,-1;1.5708rad)
FEATURE [App::Link] _XR5__R_CC25_P10_16_H_5E176B90_ln_041  label=""R10"_R_CC25_P10.16_H_5E1BADD1"
  LinkPlacement = pos=(-47.3075,40.64,0) rot=(0,0,1;1.5708rad)
  LinkedObject = -> Shape003
  Placement = pos=(-47.3075,40.64,0) rot=(0,0,1;1.5708rad)
FEATURE [App::Link] _XR5__R_CC25_P10_16_H_5E176B90_ln_042  label=""R9"_R_CC25_P10.16_H_5E1BAEED"
  LinkPlacement = pos=(-38.481,40.64,0) rot=(0,0,-1;1.5708rad)
  LinkedObject = -> Shape003
  Placement = pos=(-38.481,40.64,0) rot=(0,0,-1;1.5708rad)
FEATURE [App::Link] _XR5__R_CC25_P10_16_H_5E176B90_ln_043  label=""R8"_R_CC25_P10.16_H_5D8A07FD"
  LinkPlacement = pos=(-41.5925,40.64,0) rot=(0,0,1;1.5708rad)
  LinkedObject = -> Shape003
  Placement = pos=(-41.5925,40.64,0) rot=(0,0,1;1.5708rad)
FEATURE [App::Link] _XR5__R_CC25_P10_16_H_5E176B90_ln_044  label=""R7"_R_CC25_P10.16_H_5D8A07E6"
  LinkPlacement = pos=(-23.8125,62.23,0) rot=(0,0,1;1.5708rad)
  LinkedObject = -> Shape003
  Placement = pos=(-23.8125,62.23,0) rot=(0,0,1;1.5708rad)
FEATURE [App::Link] _XR5__R_CC25_P10_16_H_5E176B90_ln_045  label=""R6"_R_CC25_P10.16_H_5D8A07CF"
  LinkPlacement = pos=(-21.2725,60.325,0) rot=(0,0,-1;1.5708rad)
  LinkedObject = -> Shape003
  Placement = pos=(-21.2725,60.325,0) rot=(0,0,-1;1.5708rad)
FEATURE [App::Link] _XR5__R_CC25_P10_16_H_5E176B90_ln_046  label=""R5"_R_CC25_P10.16_H_5D8A07B8"
  LinkPlacement = pos=(-29.21,74.93,0) rot=(0,0,-1;1.5708rad)
  LinkedObject = -> Shape003
  Placement = pos=(-29.21,74.93,0) rot=(0,0,-1;1.5708rad)
FEATURE [App::Link] _XR5__R_CC25_P10_16_H_5E176B90_ln_047  label=""R4"_R_CC25_P10.16_H_5D8A07A1"
  LinkPlacement = pos=(-31.75,74.93,0) rot=(0,0,-1;1.5708rad)
  LinkedObject = -> Shape003
  Placement = pos=(-31.75,74.93,0) rot=(0,0,-1;1.5708rad)
FEATURE [App::Link] _XR5__R_CC25_P10_16_H_5E176B90_ln_048  label=""R3"_R_CC25_P10.16_H_5D8A078A"
  LinkPlacement = pos=(-34.29,74.93,0) rot=(0,0,-1;1.5708rad)
  LinkedObject = -> Shape003
  Placement = pos=(-34.29,74.93,0) rot=(0,0,-1;1.5708rad)
FEATURE [App::Link] _XR5__R_CC25_P10_16_H_5E176B90_ln_049  label=""R2"_R_CC25_P10.16_H_5DCDF50D"
  LinkPlacement = pos=(-44.1325,78.105,0) rot=(0,0,1;1.5708rad)
  LinkedObject = -> Shape003
  Placement = pos=(-44.1325,78.105,0) rot=(0,0,1;1.5708rad)
FEATURE [App::Link] _XR5__R_CC25_P10_16_H_5E176B90_ln_050  label=""R1"_R_CC25_P10.16_H_5DC0975F"
  LinkPlacement = pos=(-46.6725,78.105,0) rot=(0,0,-1;1.5708rad)
  LinkedObject = -> Shape003
  Placement = pos=(-46.6725,78.105,0) rot=(0,0,-1;1.5708rad)
FEATURE [Part::Feature] Shape018  label=""XQ2"_2N3904TAR_5DC00CE5"
  Placement = pos=(27.6225,29.21,0) rot=(0,0,1;1.5708rad)
  shape: bbox 3.625 x 5.54 x 10.42 mm, 233 faces (baked)
FEATURE [App::Link] _XQ2__2N3904TAR_5DC00CE5_ln_  label=""XQ1"_2N3904TAR_5DC00CD1"
  LinkPlacement = pos=(6.6675,-2.54,0) rot=(0,0,-1;1.5708rad)
  LinkedObject = -> Shape018
  Placement = pos=(6.6675,-2.54,0) rot=(0,0,-1;1.5708rad)
FEATURE [Part::Feature] Shape019  label=""XD1"_DO-41_P10.16_5DC00CBD"
  Placement = pos=(40.3225,24.765,0) rot=(0,0,1;1.5708rad)
  shape: bbox 2.395 x 11.21 x 4.985 mm, 15 faces (baked)
FEATURE [App::Link] _XD1__DO_41_P10_16_5DC00CBD_ln_  label=""XD5"_DO-41_P10.16_5DC00CAE"
  LinkPlacement = pos=(37.7825,24.765,0) rot=(0,0,-1;1.5708rad)
  LinkedObject = -> Shape019
  Placement = pos=(37.7825,24.765,0) rot=(0,0,-1;1.5708rad)
FEATURE [App::Link] _XD1__DO_41_P10_16_5DC00CBD_ln_001  label=""XD4"_DO-41_P10.16_5E361ADA"
  LinkPlacement = pos=(44.1325,17.145,0) rot=(0,0,1;0rad)
  LinkedObject = -> Shape019
  Placement = pos=(44.1325,17.145,0) rot=(0,0,1;0rad)
FEATURE [App::Link] _XD1__DO_41_P10_16_5DC00CBD_ln_002  label=""XD9"_DO-41_P10.16_5DC23218"
  LinkPlacement = pos=(40.3225,32.0675,0) rot=(0,0,1;0rad)
  LinkedObject = -> Shape019
  Placement = pos=(40.3225,32.0675,0) rot=(0,0,1;0rad)
FEATURE [App::Link] _XD1__DO_41_P10_16_5DC00CBD_ln_003  label=""XD8"_DO-41_P10.16_5DC00C81"
  LinkPlacement = pos=(40.3225,34.6075,0) rot=(0,0,1;3.14159rad)
  LinkedObject = -> Shape019
  Placement = pos=(40.3225,34.6075,0) rot=(0,0,1;3.14159rad)
FEATURE [App::Link] _XD1__DO_41_P10_16_5DC00CBD_ln_004  label=""XD7"_DO-41_P10.16_5DC00C54"
  LinkPlacement = pos=(30.7975,-3.81,0) rot=(0,0,-1;1.5708rad)
  LinkedObject = -> Shape019
  Placement = pos=(30.7975,-3.81,0) rot=(0,0,-1;1.5708rad)
FEATURE [App::Link] _XD1__DO_41_P10_16_5DC00CBD_ln_005  label=""XD6"_DO-41_P10.16_5DC00C45"
  LinkPlacement = pos=(33.3375,-3.81,0) rot=(0,0,1;1.5708rad)
  LinkedObject = -> Shape019
  Placement = pos=(33.3375,-3.81,0) rot=(0,0,1;1.5708rad)
FEATURE [App::Link] _XD1__DO_41_P10_16_5DC00CBD_ln_006  label=""XD3"_DO-41_P10.16_5DC00C36"
  LinkPlacement = pos=(35.8775,10.16,0) rot=(0,0,-1;1.5708rad)
  LinkedObject = -> Shape019
  Placement = pos=(35.8775,10.16,0) rot=(0,0,-1;1.5708rad)
FEATURE [App::Link] _XD1__DO_41_P10_16_5DC00CBD_ln_007  label=""XD2"_DO-41_P10.16_5DC00C27"
  LinkPlacement = pos=(35.8775,-3.81,0) rot=(0,0,-1;1.5708rad)
  LinkedObject = -> Shape019
  Placement = pos=(35.8775,-3.81,0) rot=(0,0,-1;1.5708rad)
FEATURE [App::Link] _XQ2__2N3904TAR_5DC00CE5_ln_001  label=""Q1"_2N3904TAR_5DD3221D"
  LinkPlacement = pos=(-18.0975,6.985,0) rot=(0,0,1;3.14159rad)
  LinkedObject = -> Shape018
  Placement = pos=(-18.0975,6.985,0) rot=(0,0,1;3.14159rad)
FEATURE [Part::Feature] Shape020  label=""C23"_FKS2G016801B00KSSD_5E2EB71B"
  Placement = pos=(47.3075,72.0725,0) rot=(0,0,-1;1.5708rad)
  shape: bbox 3.9 x 15.3 x 9.5 mm, 432 faces (baked)
FEATURE [Part::Feature] Shape021  label=""C16"_MKS2C034701C00KSSD_5D8A0691"
  Placement = pos=(23.8125,74.93,0) rot=(0,0,-1;1.5708rad)
  shape: bbox 4.65 x 15.3 x 10.5 mm, 395 faces (baked)
FEATURE [App::Link] _C16__MKS2C034701C00KSSD_5D8A0691_ln_  label=""C12"_MKS2C034701C00KSSD_5D8A0645"
  LinkPlacement = pos=(12.7,74.93,0) rot=(0,0,1;1.5708rad)
  LinkedObject = -> Shape021
  Placement = pos=(12.7,74.93,0) rot=(0,0,1;1.5708rad)
FEATURE [App::Link] _C23__FKS2G016801B00KSSD_5E2EB71B_ln_  label=""C11"_FKS2G016801B00KSSD_5DCDF616"
  LinkPlacement = pos=(9.2075,74.93,0) rot=(0,0,1;1.5708rad)
  LinkedObject = -> Shape020
  Placement = pos=(9.2075,74.93,0) rot=(0,0,1;1.5708rad)
FEATURE [App::Link] _C23__FKS2G016801B00KSSD_5E2EB71B_ln_001  label=""C10"_FKS2G016801B00KSSD_5D8B724B"
  LinkPlacement = pos=(12.3825,40.64,0) rot=(0,0,1;1.5708rad)
  LinkedObject = -> Shape020
  Placement = pos=(12.3825,40.64,0) rot=(0,0,1;1.5708rad)
FEATURE [App::Link] _C23__FKS2G016801B00KSSD_5E2EB71B_ln_002  label=""C9"_FKS2G016801B00KSSD_5D8B7215"
  LinkPlacement = pos=(2.2225,40.64,0) rot=(0,0,-1;1.5708rad)
  LinkedObject = -> Shape020
  Placement = pos=(2.2225,40.64,0) rot=(0,0,-1;1.5708rad)
FEATURE [App::Link] _C23__FKS2G016801B00KSSD_5E2EB71B_ln_003  label=""C8"_FKS2G016801B00KSSD_5D8B71DF"
  LinkPlacement = pos=(-15.5575,40.64,0) rot=(0,0,-1;1.5708rad)
  LinkedObject = -> Shape020
  Placement = pos=(-15.5575,40.64,0) rot=(0,0,-1;1.5708rad)
FEATURE [App::Link] _C23__FKS2G016801B00KSSD_5E2EB71B_ln_004  label=""C7"_FKS2G016801B00KSSD_5D8B71A9"
  LinkPlacement = pos=(-25.4,40.64,0) rot=(0,0,-1;1.5708rad)
  LinkedObject = -> Shape020
  Placement = pos=(-25.4,40.64,0) rot=(0,0,-1;1.5708rad)
FEATURE [App::Link] _C23__FKS2G016801B00KSSD_5E2EB71B_ln_005  label=""C6"_FKS2G016801B00KSSD_5D8A05D3"
  LinkPlacement = pos=(-44.45,40.64,0) rot=(0,0,-1;1.5708rad)
  LinkedObject = -> Shape020
  Placement = pos=(-44.45,40.64,0) rot=(0,0,-1;1.5708rad)
FEATURE [Part::Feature] Shape022  label=""C5"_FKS2G013301A00KSSD_5D8A05C0"
  Placement = pos=(-18.0975,60.365,0) rot=(0,0,-1;1.5708rad)
  shape: bbox 3.15 x 15.3 x 8.5 mm, 428 faces (baked)
FEATURE [Part::Feature] Shape023  label=""C4"_FKS2G011001A00KSSD_5D8A05AD"
  Placement = pos=(-26.67,74.93,0) rot=(0,0,1;1.5708rad)
  shape: bbox 3.15 x 15.3 x 8.5 mm, 398 faces (baked)
FEATURE [Part::Feature] Shape024  label=""C3"_MKS2C031001A00KSSD_5D8A059A"
  Placement = pos=(-36.83,74.93,0) rot=(0,0,-1;1.5708rad)
  shape: bbox 3.15 x 15.3 x 8.5 mm, 403 faces (baked)
FEATURE [Part::Feature] Shape025  label=""C1"_MKS2F024701C00KSSD_5DED55F5"
  Placement = pos=(-49.8475,78.105,0) rot=(0,0,1;1.5708rad)
  shape: bbox 4.65 x 15.3 x 10.5 mm, 401 faces (baked)
FEATURE [App::Part] Top_3323
  Group = -> [Shape,_Z6__RC4558P_5E32D110_ln_,_Z6__RC4558P_5E32D110_ln_001,Shape003,_Z6__RC4558P_5E32D110_ln_002,_Z6__RC4558P_5E32D110_ln_003,Shape004,_JP16__R_0R_Wire_Jumper_P10_16_5D8DF354_ln_,_JP16__R_0R_Wire_Jumper_P10_16_5D8DF354_ln_001,_JP16__R_0R_Wire_Jumper_P10_16_5D8DF354_ln_002,_JP16__R_0R_Wire_Jumper_P10_16_5D8DF354_ln_003,_JP16__R_0R_Wire_Jumper_P10_16_5D8DF354_ln_004,+110 more]
  Origin = -> Origin003
FEATURE [Part::Feature] Shape006  label=""XJP1"_R_0603_1608M_5E0F142D"
  Placement = pos=(39.0525,10.16,-1.6) rot=(0.707107,0.707107,0;3.14159rad)
  shape: bbox 0.8 x 1.6 x 0.45 mm, 22 faces (baked)
FEATURE [App::Part] Bot_3323
  Group = -> [Shape006]
  Origin = -> Origin004
FEATURE [App::Part] Step_Models_3323
  Group = -> [Top_3323,Bot_3323]
  Origin = -> Origin002
FEATURE [Part::Feature] Shape002  label=""H_A6"_Hex_Spacer_FF_M3x12_FF4.7_5DE407FA"
  Placement = pos=(52.705,67.31,0) rot=(0,0,1;0rad)
  shape: bbox 4.7 x 5.427 x 12 mm, 9 faces (baked)
FEATURE [App::Link] _H_A6__Hex_Spacer_FF_M3x12_FF4_7_5DE407FA_ln_  label=""H_A5"_A6"_Hex_Spacer_FF_M3x12_FF4.7_5DEEC540"
  LinkPlacement = pos=(52.705,8.255,0) rot=(0,0,1;0rad)
  LinkedObject = -> Shape002
  Placement = pos=(52.705,8.255,0) rot=(0,0,1;0rad)
FEATURE [App::Link] _H_A6__Hex_Spacer_FF_M3x12_FF4_7_5DE407FA_ln_001  label=""H_A4"_A6"_Hex_Spacer_FF_M3x12_FF4.7_5DE5300C"
  LinkPlacement = pos=(-52.705,67.31,0) rot=(0,0,1;0rad)
  LinkedObject = -> Shape002
  Placement = pos=(-52.705,67.31,0) rot=(0,0,1;0rad)
FEATURE [App::Link] _H_A6__Hex_Spacer_FF_M3x12_FF4_7_5DE407FA_ln_002  label=""H_A2"_A6"_Hex_Spacer_FF_M3x12_FF4.7_5DD266E3"
  LinkPlacement = pos=(-52.705,8.255,0) rot=(0,0,1;0rad)
  LinkedObject = -> Shape002
  Placement = pos=(-52.705,8.255,0) rot=(0,0,1;0rad)
FEATURE [App::Part] TopV_3323
  Group = -> [Shape002,_H_A6__Hex_Spacer_FF_M3x12_FF4_7_5DE407FA_ln_,_H_A6__Hex_Spacer_FF_M3x12_FF4_7_5DE407FA_ln_001,_H_A6__Hex_Spacer_FF_M3x12_FF4_7_5DE407FA_ln_002]
  Origin = -> Origin006
FEATURE [App::Part] Step_Virtual_Models_3323
  Group = -> [TopV_3323]
  Origin = -> Origin005
FEATURE [App::Part] Board_3323  label="#110-000-S1A - Phasor PCB"
  Group = -> [Board_Geoms_3323,Step_Models_3323,Step_Virtual_Models_3323]
  Origin = -> Origin001
